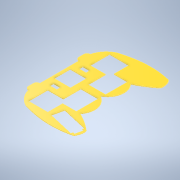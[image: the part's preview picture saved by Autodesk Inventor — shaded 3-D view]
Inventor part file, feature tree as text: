
AUTODESK INVENTOR PART (.ipt)
format: ipt  version: 2022 (Build 260153000, 153)  size: 311,808 bytes
history: native  units: mm
features: sketch x2, extrude x1
ambient origin geometry x8: Origin, YZ Plane, XZ Plane, XY Plane, X Axis, Y Axis, Z Axis, Center Point
bodies: Solid1 (feature_tree)
feature tree (3):
  sketch  "Sketch1"  dims[d0=35.0mm d1=60.0mm]
  extrude  "Extrusion1"  Depth=60.0mm
  sketch  "Sketch2"  dims[d2=17.5mm d3=25.0mm d4=22.5mm d6=25.0mm d7=27.0mm d8=34.0mm d9=27.0mm d10=7.5mm d11=25.0mm d12=27.0mm d13=34.0mm d14=27.0mm d15=6.0mm d16=6.0mm d17=6.0mm d18=6.5mm d22=6.0mm d23=40.0mm d25=360.0deg d27=25.0mm d28=27.0mm d31=40.0mm d32=25.0mm d33=27.0mm d34=5.0mm d35=8.0mm d36=8.0mm d37=35.0mm d38=8.0mm d39=12.0mm d40=8.0mm d41=60.0mm d42=17.5mm d47=4.0mm d48=7.5mm d49=22.5mm d50=25.0mm d51=27.0mm d52=34.0mm d53=6.5mm d54=3.0mm d55=3.0mm d56=6.0mm d57=6.0mm d58=40.0mm d60=360.0deg d62=50.0mm d63=1.0mm d64=0.0mm d65=1.5mm d66=12.5mm d67=27.0mm d68=25.0mm d69=1.401mm d70=13.425896mm d71=200.0mm d72=37.3mm d73=4.0mm d74=37.3mm d75=15.0mm d76=15.0mm d77=30.0mm d78=30.0mm d79=48.0mm d80=9.0mm d81=9.0mm d82=3.0mm d83=3.0mm d84=3.0mm d85=3.0mm d86=6.5mm d87=14.0mm d88=3.0mm d89=1.5mm d90=1.5mm d91=3.0mm]
